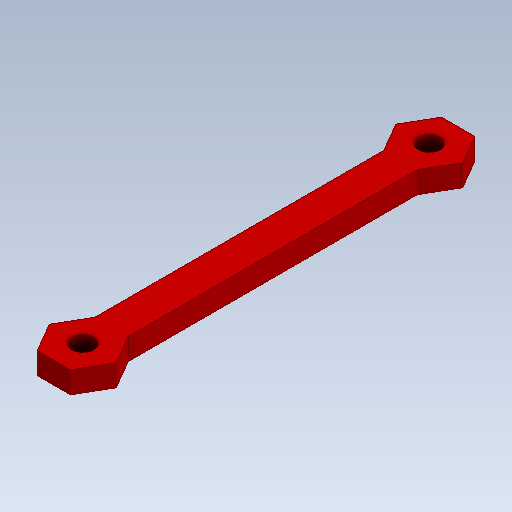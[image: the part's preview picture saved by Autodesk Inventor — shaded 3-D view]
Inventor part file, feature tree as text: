
AUTODESK INVENTOR PART (.ipt)
format: ipt  version: 2020 (Build 240168000, 168)  size: 126,976 bytes
history: native  units: in
note: dims shown in document units (in); Inventor stores cm internally (conversion verified against a paired STEP export)
features: extrude x1, sketch x1
ambient origin geometry x8: Origin, YZ Plane, XZ Plane, XY Plane, X Axis, Y Axis, Z Axis, Center Point
bodies: Solid1 (feature_tree)
feature tree (2):
  extrude  "Extrusion1"  Depth=0.315in
  sketch  "Sketch1"  dims[d1=1.5748in d2=0.315in d3=0.122in d4=0.122in d5=0.1181in d6=0.0in]
